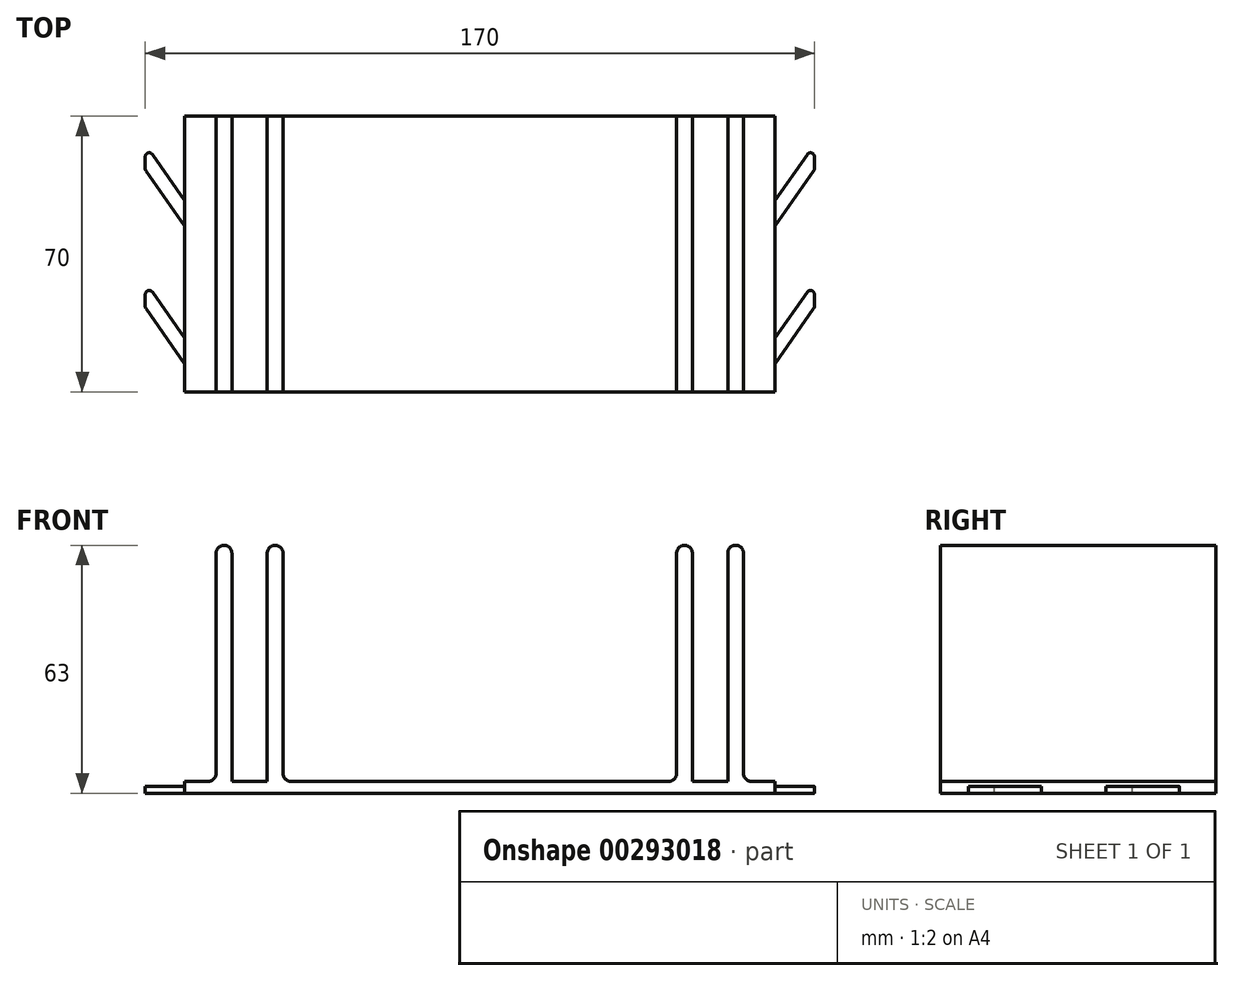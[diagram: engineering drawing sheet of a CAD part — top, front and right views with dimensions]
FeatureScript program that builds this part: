
annotation { "Feature Type Name" : "Feature", "Feature Type Description" : "" }
export const myFeature = defineFeature(function(context is Context, id is Id, definition is map)
    precondition{}
    {
        {
            var Q0;
            Q0=qCreatedBy(makeId("Front.planeOp"),FACE);
            var sketch = newSketch(context, id + "F0", { "sketchPlane" : qUnion([Q0])});
            skLineSegment(sketch, "E0.bottom", {"start": v(0, -23) * mm, "end": v(75, -23) * mm});
            skLineSegment(sketch, "E0.top", {"start": v(0, -20) * mm, "end": v(75, -20) * mm});
            skLineSegment(sketch, "E0.left", {"start": v(0, -23) * mm, "end": v(0, -20) * mm});
            skLineSegment(sketch, "E0.right", {"start": v(75, -23) * mm, "end": v(75, -20) * mm});
            skLineSegment(sketch, "E1", {"start": v(0, 0) * mm, "end": v(0, -20) * mm, "construction": true});
            skLineSegment(sketch, "E2", {"start": v(75, -21.5) * mm, "end": v(67, -21.5) * mm, "construction": true});
            skPoint(sketch, "E2.endSnap0", {"position": v(75, -21.5) * mm});
            skLineSegment(sketch, "E3", {"start": v(67, -21.5) * mm, "end": v(65, -21.5) * mm, "construction": true});
            skLineSegment(sketch, "E4", {"start": v(65, -21.5) * mm, "end": v(63, -21.5) * mm, "construction": true});
            skLineSegment(sketch, "E5", {"start": v(63, -21.5) * mm, "end": v(54, -21.5) * mm, "construction": true});
            skLineSegment(sketch, "E6", {"start": v(54, -21.5) * mm, "end": v(50, -21.5) * mm, "construction": true});
            skLineSegment(sketch, "E7", {"start": v(50, -21.5) * mm, "end": v(0, -21.5) * mm, "construction": true});
            skLineSegment(sketch, "E8", {"start": v(65, -21.5) * mm, "end": v(65, -23) * mm, "construction": true});
            skLineSegment(sketch, "E9", {"start": v(65, -23) * mm, "end": v(65, -21) * mm});
            skPoint(sketch, "E9.endSnap0", {"position": v(65, -22.25) * mm});
            skLineSegment(sketch, "E10", {"start": v(65, -21) * mm, "end": v(75, -21) * mm});
            skLineSegment(sketch, "E11", {"start": v(65, -22.25) * mm, "end": v(71, -22.25) * mm, "construction": true});
            skLineSegment(sketch, "E12", {"start": v(71, -22.25) * mm, "end": v(71, -23) * mm});
            skLineSegment(sketch, "E13", {"start": v(71, -23) * mm, "end": v(71, -21) * mm});
            skLineSegment(sketch, "E14", {"start": v(67, -21.5) * mm, "end": v(67, 40) * mm});
            skLineSegment(sketch, "E15", {"start": v(63, 40) * mm, "end": v(63, -21.5) * mm});
            skLineSegment(sketch, "E16", {"start": v(63, 40) * mm, "end": v(67, 40) * mm});
            skLineSegment(sketch, "E17", {"start": v(54, -21.5) * mm, "end": v(54, 40) * mm});
            skLineSegment(sketch, "E18", {"start": v(54, 40) * mm, "end": v(50, 40) * mm});
            skLineSegment(sketch, "E19", {"start": v(50, 40) * mm, "end": v(50, -21.5) * mm});
            skLineSegment(sketch, "E20.MirrorCS", {"start": v(-65, -23) * mm, "end": v(-65, -21) * mm});
            skLineSegment(sketch, "E21.MirrorCS", {"start": v(-65, -21.5) * mm, "end": v(-65, -23) * mm, "construction": true});
            skLineSegment(sketch, "E22.MirrorCS", {"start": v(-67, -21.5) * mm, "end": v(-65, -21.5) * mm, "construction": true});
            skLineSegment(sketch, "E23.MirrorCS", {"start": v(-65, -21.5) * mm, "end": v(-63, -21.5) * mm, "construction": true});
            skLineSegment(sketch, "E24.MirrorCS", {"start": v(-71, -23) * mm, "end": v(-71, -21) * mm});
            skLineSegment(sketch, "E25.MirrorCS", {"start": v(-71, -22.25) * mm, "end": v(-71, -23) * mm});
            skLineSegment(sketch, "E26.MirrorCS", {"start": v(-75, -23) * mm, "end": v(-75, -20) * mm});
            skLineSegment(sketch, "E27.MirrorCS", {"start": v(-75, -21.5) * mm, "end": v(-67, -21.5) * mm, "construction": true});
            skLineSegment(sketch, "E28.MirrorCS", {"start": v(-65, -21) * mm, "end": v(-75, -21) * mm});
            skLineSegment(sketch, "E29.MirrorCS", {"start": v(-65, -22.25) * mm, "end": v(-71, -22.25) * mm, "construction": true});
            skPoint(sketch, "E30.MirrorP", {"position": v(-75, -21.5) * mm});
            skLineSegment(sketch, "E31.MirrorCS", {"start": v(-63, -21.5) * mm, "end": v(-54, -21.5) * mm, "construction": true});
            skPoint(sketch, "E32.MirrorP", {"position": v(-65, -22.25) * mm});
            skLineSegment(sketch, "E33.MirrorCS", {"start": v(-54, -21.5) * mm, "end": v(-50, -21.5) * mm, "construction": true});
            skLineSegment(sketch, "E34.MirrorCS", {"start": v(-54, 40) * mm, "end": v(-50, 40) * mm});
            skLineSegment(sketch, "E35.MirrorCS", {"start": v(-63, 40) * mm, "end": v(-67, 40) * mm});
            skLineSegment(sketch, "E36.MirrorCS", {"start": v(0, -23) * mm, "end": v(-75, -23) * mm});
            skLineSegment(sketch, "E37.MirrorCS", {"start": v(-63, 40) * mm, "end": v(-63, -21.5) * mm});
            skLineSegment(sketch, "E38.MirrorCS", {"start": v(-50, 40) * mm, "end": v(-50, -21.5) * mm});
            skLineSegment(sketch, "E39.MirrorCS", {"start": v(-67, -21.5) * mm, "end": v(-67, 40) * mm});
            skLineSegment(sketch, "E40.MirrorCS", {"start": v(0, -20) * mm, "end": v(-75, -20) * mm});
            skLineSegment(sketch, "E41.MirrorCS", {"start": v(-50, -21.5) * mm, "end": v(0, -21.5) * mm, "construction": true});
            skLineSegment(sketch, "E42.MirrorCS", {"start": v(-54, -21.5) * mm, "end": v(-54, 40) * mm});
            skSolve(sketch);
        }
        {
            var Q0;
            {var subQ0=sQuery(id+"F0.wireOp",EDGE,"E35.MirrorCS");Q0=makeQuery(id+"F0.imprint","IMPRINT",FACE,{"disambiguationData":[TD([[makeQuery(id+"F0.imprint","IMPRINT",EDGE,{"derivedFrom":subQ0}),1.0]])]});}
            var Q1;
            {var subQ0=sQuery(id+"F0.wireOp",EDGE,"E34.MirrorCS");Q1=makeQuery(id+"F0.imprint","IMPRINT",FACE,{"disambiguationData":[TD([[makeQuery(id+"F0.imprint","IMPRINT",EDGE,{"derivedFrom":subQ0}),-1.0]])]});}
            var Q2;
            {var subQ5=sQuery(id+"F0.wireOp",EDGE,"E18");Q2=makeQuery(id+"F0.imprint","IMPRINT",FACE,{"disambiguationData":[TD([[makeQuery(id+"F0.imprint","IMPRINT",EDGE,{"derivedFrom":subQ5}),1.0]])]});}
            var Q3;
            {var subQ5=sQuery(id+"F0.wireOp",EDGE,"E16");Q3=makeQuery(id+"F0.imprint","IMPRINT",FACE,{"disambiguationData":[TD([[makeQuery(id+"F0.imprint","IMPRINT",EDGE,{"derivedFrom":subQ5}),-1.0]])]});}
            var Q4;
            {var subQ10=sQuery(id+"F0.wireOp",EDGE,"E9");Q4=makeQuery(id+"F0.imprint","IMPRINT",FACE,{"disambiguationData":[TD([[makeQuery(id+"F0.imprint","IMPRINT",EDGE,{"derivedFrom":subQ10}),1.0]])]});}
            var Q5;
            {var subQ1=sQuery(id+"F0.wireOp",EDGE,"E0.right");var subQ4=sQuery(id+"F0.wireOp",EDGE,"E0.top");var subQ5=makeQuery(id+"F0.imprint","INTERSECT",VERTEX,{"derivedFrom":[subQ4,subQ1]});Q5=makeQuery(id+"F0.imprint","IMPRINT",FACE,{"disambiguationData":[TD([[makeQuery(id+"F0.imprint","IMPRINT",EDGE,{"disambiguationData":[TD([[subQ5,1.0]])],"derivedFrom":subQ4}),-1.0]])]});}
            var Q6;
            {var subQ4=sQuery(id+"F0.wireOp",EDGE,"E9");Q6=makeQuery(id+"F0.imprint","IMPRINT",FACE,{"disambiguationData":[TD([[makeQuery(id+"F0.imprint","IMPRINT",EDGE,{"derivedFrom":subQ4}),-1.0]])]});}
            var Q7;
            {var subQ0=sQuery(id+"F0.wireOp",EDGE,"E13");var subQ3=makeQuery(id+"F0.imprint","IMPRINT",VERTEX,{"derivedFrom":subQ0});Q7=makeQuery(id+"F0.imprint","IMPRINT",FACE,{"disambiguationData":[TD([[makeQuery(id+"F0.imprint","IMPRINT",EDGE,{"disambiguationData":[TD([[subQ3,1.0]])],"derivedFrom":subQ0}),-1.0]])]});}
            var Q8;
            {var subQ6=sQuery(id+"F0.wireOp",EDGE,"E0.left");Q8=makeQuery(id+"F0.imprint","IMPRINT",FACE,{"disambiguationData":[TD([[makeQuery(id+"F0.imprint","IMPRINT",EDGE,{"derivedFrom":subQ6}),1.0]])]});}
            var Q9;
            {var subQ1=sQuery(id+"F0.wireOp",EDGE,"E28.MirrorCS");var subQ8=makeQuery(id+"F0.imprint","INTERSECT",VERTEX,{"derivedFrom":[sQuery(id+"F0.wireOp",EDGE,"E24.MirrorCS"),subQ1]});Q9=makeQuery(id+"F0.imprint","IMPRINT",FACE,{"disambiguationData":[TD([[makeQuery(id+"F0.imprint","IMPRINT",EDGE,{"disambiguationData":[TD([[subQ8,1.0]])],"derivedFrom":subQ1}),-1.0]])]});}
            var Q10;
            {var subQ1=sQuery(id+"F0.wireOp",EDGE,"E24.MirrorCS");var subQ5=makeQuery(id+"F0.imprint","IMPRINT",VERTEX,{"derivedFrom":subQ1});Q10=makeQuery(id+"F0.imprint","IMPRINT",FACE,{"disambiguationData":[TD([[makeQuery(id+"F0.imprint","IMPRINT",EDGE,{"disambiguationData":[TD([[subQ5,1.0]])],"derivedFrom":subQ1}),1.0]])]});}
            var Q11;
            {var subQ1=sQuery(id+"F0.wireOp",EDGE,"E20.MirrorCS");Q11=makeQuery(id+"F0.imprint","IMPRINT",FACE,{"disambiguationData":[TD([[makeQuery(id+"F0.imprint","IMPRINT",EDGE,{"derivedFrom":subQ1}),1.0]])]});}
            extrude(context, id + "F1", {"entities" : qUnion([Q0, Q1, Q2, Q3, Q4, Q5, Q6, Q7, Q8, Q9, Q10, Q11]), "depth" : 70 * mm});
        }
        {
            var Q0;
            Q0=makeQuery(id+"F1.opExtrude","SWEPT_EDGE",EDGE,{"disambiguationData":[OSD([sQuery(id+"F0.wireOp",EDGE,"E35.MirrorCS"),sQuery(id+"F0.wireOp",EDGE,"E39.MirrorCS")])]});
            var Q1;
            Q1=makeQuery(id+"F1.opExtrude","SWEPT_EDGE",EDGE,{"disambiguationData":[OSD([sQuery(id+"F0.wireOp",EDGE,"E35.MirrorCS"),sQuery(id+"F0.wireOp",EDGE,"E37.MirrorCS")])]});
            var Q2;
            Q2=makeQuery(id+"F1.opExtrude","SWEPT_EDGE",EDGE,{"disambiguationData":[OSD([sQuery(id+"F0.wireOp",EDGE,"E34.MirrorCS"),sQuery(id+"F0.wireOp",EDGE,"E42.MirrorCS")])]});
            var Q3;
            Q3=makeQuery(id+"F1.opExtrude","SWEPT_EDGE",EDGE,{"disambiguationData":[OSD([sQuery(id+"F0.wireOp",EDGE,"E34.MirrorCS"),sQuery(id+"F0.wireOp",EDGE,"E38.MirrorCS")])]});
            var Q4;
            Q4=makeQuery(id+"F1.opExtrude","SWEPT_EDGE",EDGE,{"disambiguationData":[OSD([sQuery(id+"F0.wireOp",EDGE,"E17"),sQuery(id+"F0.wireOp",EDGE,"E18")])]});
            var Q5;
            Q5=makeQuery(id+"F1.opExtrude","SWEPT_EDGE",EDGE,{"disambiguationData":[OSD([sQuery(id+"F0.wireOp",EDGE,"E18"),sQuery(id+"F0.wireOp",EDGE,"E19")])]});
            var Q6;
            Q6=makeQuery(id+"F1.opExtrude","SWEPT_EDGE",EDGE,{"disambiguationData":[OSD([sQuery(id+"F0.wireOp",EDGE,"E15"),sQuery(id+"F0.wireOp",EDGE,"E16")])]});
            var Q7;
            Q7=makeQuery(id+"F1.opExtrude","SWEPT_EDGE",EDGE,{"disambiguationData":[OSD([sQuery(id+"F0.wireOp",EDGE,"E14"),sQuery(id+"F0.wireOp",EDGE,"E16")])]});
            fillet(context, id + "F2", {"entities" : qUnion([Q0, Q1, Q2, Q3, Q4, Q5, Q6, Q7]), "radius" : 2 * mm, "tangentPropagation" : true, "allowEdgeOverflow" : false});
        }
        {
            var Q0;
            Q0=makeQuery(id+"F1.opExtrude","SWEPT_EDGE",EDGE,{"disambiguationData":[OSD([sQuery(id+"F0.wireOp",EDGE,"E38.MirrorCS"),sQuery(id+"F0.wireOp",EDGE,"E40.MirrorCS")])]});
            var Q1;
            Q1=makeQuery(id+"F1.opExtrude","SWEPT_EDGE",EDGE,{"disambiguationData":[OSD([sQuery(id+"F0.wireOp",EDGE,"E0.top"),sQuery(id+"F0.wireOp",EDGE,"E19")])]});
            var Q2;
            Q2=makeQuery(id+"F1.opExtrude","SWEPT_EDGE",EDGE,{"disambiguationData":[OSD([sQuery(id+"F0.wireOp",EDGE,"E39.MirrorCS"),sQuery(id+"F0.wireOp",EDGE,"E40.MirrorCS")])]});
            var Q3;
            Q3=makeQuery(id+"F1.opExtrude","SWEPT_EDGE",EDGE,{"disambiguationData":[OSD([sQuery(id+"F0.wireOp",EDGE,"E0.top"),sQuery(id+"F0.wireOp",EDGE,"E14")])]});
            fillet(context, id + "F3", {"entities" : qUnion([Q0, Q1, Q2, Q3]), "radius" : 2 * mm, "tangentPropagation" : true, "allowEdgeOverflow" : false});
        }
        {
            var Q0;
            Q0=makeQuery(id+"F1.opExtrude","SWEPT_FACE",FACE,{"disambiguationData":[OSD([sQuery(id+"F0.wireOp",EDGE,"E0.bottom"),sQuery(id+"F0.wireOp",EDGE,"E36.MirrorCS")])]});
            var sketch = newSketch(context, id + "F4", { "sketchPlane" : qUnion([Q0])});
            skLineSegment(sketch, "E43", {"start": v(75, 0) * mm, "end": v(-75, 0) * mm, "construction": true});
            skLineSegment(sketch, "E44", {"start": v(-75, 0) * mm, "end": v(-75, 70) * mm, "construction": true});
            skLineSegment(sketch, "E45", {"start": v(-75, 70) * mm, "end": v(75, 70) * mm, "construction": true});
            skLineSegment(sketch, "E46", {"start": v(75, 70) * mm, "end": v(75, 0) * mm, "construction": true});
            skLineSegment(sketch, "E47", {"start": v(75, 35) * mm, "end": v(-75, 35) * mm});
            skLineSegment(sketch, "E48", {"start": v(85, 35) * mm, "end": v(85, 0) * mm, "construction": true});
            skLineSegment(sketch, "E49", {"start": v(0, 70) * mm, "end": v(0, 0) * mm});
            skLineSegment(sketch, "E50", {"start": v(75, 35) * mm, "end": v(75, 27.9) * mm, "construction": true});
            skLineSegment(sketch, "E51", {"start": v(75, 27.9) * mm, "end": v(75, 7.1) * mm, "construction": true});
            skLineSegment(sketch, "E52", {"start": v(75, 27.9) * mm, "end": v(85, 13.62) * mm});
            skLineSegment(sketch, "E53", {"start": v(85, 13.62) * mm, "end": v(85, 7.1) * mm});
            skLineSegment(sketch, "E54", {"start": v(85, 7.1) * mm, "end": v(75, 21.38) * mm});
            skLineSegment(sketch, "E55", {"start": v(85, 7.1) * mm, "end": v(75, 7.1) * mm, "construction": true});
            skLineSegment(sketch, "E56.MirrorCS", {"start": v(-85, 13.62) * mm, "end": v(-85, 7.1) * mm});
            skLineSegment(sketch, "E57.MirrorCS", {"start": v(-85, 7.1) * mm, "end": v(-75, 7.1) * mm, "construction": true});
            skLineSegment(sketch, "E58.MirrorCS", {"start": v(-85, 7.1) * mm, "end": v(-75, 21.38) * mm});
            skLineSegment(sketch, "E59.MirrorCS", {"start": v(-85, 35) * mm, "end": v(-85, 0) * mm, "construction": true});
            skLineSegment(sketch, "E60.MirrorCS", {"start": v(-75, 35) * mm, "end": v(-75, 27.9) * mm, "construction": true});
            skLineSegment(sketch, "E61.MirrorCS", {"start": v(-75, 27.9) * mm, "end": v(-75, 7.1) * mm, "construction": true});
            skLineSegment(sketch, "E62.MirrorCS", {"start": v(-75, 27.9) * mm, "end": v(-85, 13.62) * mm});
            skLineSegment(sketch, "E63.MirrorCS", {"start": v(-75, 35) * mm, "end": v(75, 35) * mm});
            skLineSegment(sketch, "E64.MirrorCS", {"start": v(-75, 42.1) * mm, "end": v(-75, 62.9) * mm, "construction": true});
            skLineSegment(sketch, "E65.MirrorCS", {"start": v(85, 62.9) * mm, "end": v(75, 62.9) * mm, "construction": true});
            skLineSegment(sketch, "E66.MirrorCS", {"start": v(75, 42.1) * mm, "end": v(75, 62.9) * mm, "construction": true});
            skLineSegment(sketch, "E67.MirrorCS", {"start": v(85, 56.38) * mm, "end": v(85, 62.9) * mm});
            skLineSegment(sketch, "E68.MirrorCS", {"start": v(85, 35) * mm, "end": v(85, 70) * mm, "construction": true});
            skLineSegment(sketch, "E69", {"start": v(75, 56.38) * mm, "end": v(85, 42.1) * mm});
            skLineSegment(sketch, "E70", {"start": v(85, 48.62) * mm, "end": v(75, 62.9) * mm});
            skLineSegment(sketch, "E71", {"start": v(75, 62.9) * mm, "end": v(75, 56.38) * mm, "construction": true});
            skLineSegment(sketch, "E72.MirrorCS", {"start": v(-85, 56.38) * mm, "end": v(-85, 62.9) * mm});
            skLineSegment(sketch, "E73.MirrorCS", {"start": v(-75, 62.9) * mm, "end": v(-75, 56.38) * mm, "construction": true});
            skLineSegment(sketch, "E74.MirrorCS", {"start": v(-75, 56.38) * mm, "end": v(-85, 42.1) * mm});
            skLineSegment(sketch, "E75.MirrorCS", {"start": v(-85, 62.9) * mm, "end": v(-75, 62.9) * mm, "construction": true});
            skLineSegment(sketch, "E76.MirrorCS", {"start": v(-85, 35) * mm, "end": v(-85, 70) * mm, "construction": true});
            skLineSegment(sketch, "E77.MirrorCS", {"start": v(-85, 48.62) * mm, "end": v(-75, 62.9) * mm});
            skLineSegment(sketch, "E78", {"start": v(85, 48.62) * mm, "end": v(85, 42.1) * mm});
            skLineSegment(sketch, "E79", {"start": v(75, 62.9) * mm, "end": v(75, 56.38) * mm});
            skLineSegment(sketch, "E80", {"start": v(-85, 48.62) * mm, "end": v(-85, 42.1) * mm});
            skLineSegment(sketch, "E81", {"start": v(-75, 62.9) * mm, "end": v(-75, 56.38) * mm});
            skSolve(sketch);
        }
        {
            var Q0;
            Q0=makeQuery(id+"F4.imprint","IMPRINT",FACE,{"disambiguationData":[TD([[makeQuery(id+"F4.imprint","IMPRINT",EDGE,{"derivedFrom":sQuery(id+"F4.wireOp",EDGE,"E74.MirrorCS")}),-1.0]])]});
            var Q1;
            Q1=makeQuery(id+"F4.imprint","IMPRINT",FACE,{"disambiguationData":[TD([[makeQuery(id+"F4.imprint","IMPRINT",EDGE,{"derivedFrom":sQuery(id+"F4.wireOp",EDGE,"E56.MirrorCS")}),1.0]])]});
            var Q2;
            {var subQ0=sQuery(id+"F4.wireOp",EDGE,"E52");Q2=makeQuery(id+"F4.imprint","IMPRINT",FACE,{"disambiguationData":[TD([[makeQuery(id+"F4.imprint","IMPRINT",EDGE,{"derivedFrom":subQ0}),-1.0]])]});}
            var Q3;
            Q3=makeQuery(id+"F4.imprint","IMPRINT",FACE,{"disambiguationData":[TD([[makeQuery(id+"F4.imprint","IMPRINT",EDGE,{"derivedFrom":sQuery(id+"F4.wireOp",EDGE,"E69")}),1.0]])]});
            extrude(context, id + "F5", {"entities" : qUnion([Q0, Q1, Q2, Q3]), "operationType" : NewBodyOperationType.ADD, "oppositeDirection" : true, "depth" : 1.8 * mm});
        }
        {
            var Q0;
            Q0=makeQuery(id+"F5.opExtrude","SWEPT_EDGE",EDGE,{"disambiguationData":[OSD([sQuery(id+"F4.wireOp",EDGE,"E69"),sQuery(id+"F4.wireOp",EDGE,"E78")])]});
            var Q1;
            Q1=makeQuery(id+"F5.opExtrude","SWEPT_EDGE",EDGE,{"disambiguationData":[OSD([sQuery(id+"F4.wireOp",EDGE,"E53"),sQuery(id+"F4.wireOp",EDGE,"E54")])]});
            var Q2;
            Q2=makeQuery(id+"F5.opExtrude","SWEPT_EDGE",EDGE,{"disambiguationData":[OSD([sQuery(id+"F4.wireOp",EDGE,"E52"),sQuery(id+"F4.wireOp",EDGE,"E53")])]});
            var Q3;
            Q3=makeQuery(id+"F5.opExtrude","SWEPT_EDGE",EDGE,{"disambiguationData":[OSD([sQuery(id+"F4.wireOp",EDGE,"E70"),sQuery(id+"F4.wireOp",EDGE,"E78")])]});
            var Q4;
            Q4=makeQuery(id+"F5.opExtrude","SWEPT_EDGE",EDGE,{"disambiguationData":[OSD([sQuery(id+"F4.wireOp",EDGE,"E56.MirrorCS"),sQuery(id+"F4.wireOp",EDGE,"E58.MirrorCS")])]});
            var Q5;
            Q5=makeQuery(id+"F5.opExtrude","SWEPT_EDGE",EDGE,{"disambiguationData":[OSD([sQuery(id+"F4.wireOp",EDGE,"E56.MirrorCS"),sQuery(id+"F4.wireOp",EDGE,"E62.MirrorCS")])]});
            var Q6;
            Q6=makeQuery(id+"F5.opExtrude","SWEPT_EDGE",EDGE,{"disambiguationData":[OSD([sQuery(id+"F4.wireOp",EDGE,"E74.MirrorCS"),sQuery(id+"F4.wireOp",EDGE,"E80")])]});
            var Q7;
            Q7=makeQuery(id+"F5.opExtrude","SWEPT_EDGE",EDGE,{"disambiguationData":[OSD([sQuery(id+"F4.wireOp",EDGE,"E77.MirrorCS"),sQuery(id+"F4.wireOp",EDGE,"E80")])]});
            fillet(context, id + "F6", {"entities" : qUnion([Q0, Q1, Q2, Q3, Q4, Q5, Q6, Q7]), "radius" : 1 * mm, "tangentPropagation" : true, "allowEdgeOverflow" : false});
        }
    });
